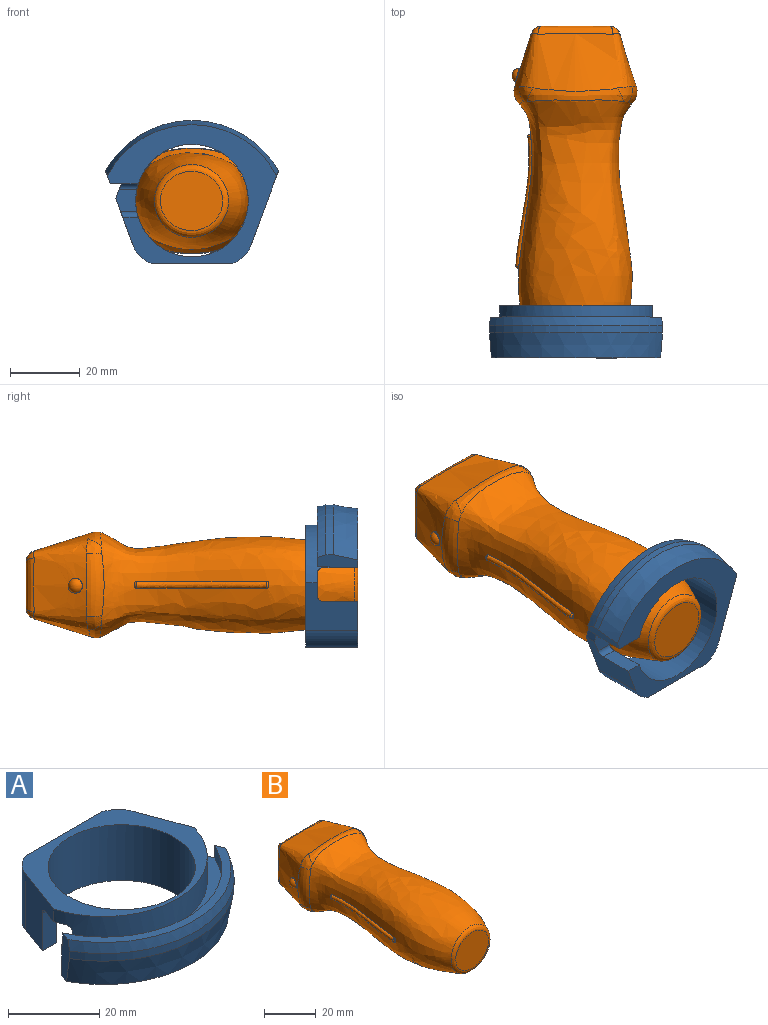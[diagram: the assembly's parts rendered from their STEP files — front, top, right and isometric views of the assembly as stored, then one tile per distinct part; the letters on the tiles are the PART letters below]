
ASSEMBLY  parts=2 mates=1
PART A: 21 faces, bbox 50.6x40.9x15 mm
  f0: plane 43.64x35.03mm, normal (0,0,1), area 388.7mm2, adj f2,f14,f16,f17,f18,f19,f20
  f1: cylinder r=28.52mm len=49.53mm, axis (0,0,1), area 121.9mm2, adj f7,f8,f15,f16
  f2: cylinder r=22.68mm len=43.64mm, axis (0,0,1), area 377.4mm2, adj f0,f5,f10,f11,f13,f16,f17
  f3: plane 48.95x17.13mm, normal (0,0,1), area 120.6mm2, adj f4,f7,f15,f16
  f4: cylinder r=25.86mm len=47.02mm, axis (0,0,1), area 200.9mm2, adj f3,f5,f15,f16
  f5: plane 47.02x19.67mm, normal (0,0,1), area 180.1mm2, adj f2,f4,f13,f15,f16
  f6: plane 48.44x39.68mm, normal (0,0,-1), area 607.5mm2, adj f8,f12,f13,f14,f15,f16,f17,f18
  f7: cone r=28.52mm half-angle=14deg, axis (0,0,-1), area 156.7mm2, adj f1,f3,f15,f16
  f8: cone r=28.52mm half-angle=9.5deg, axis (0,0,1), area 430.8mm2, adj f1,f6,f15,f16
  f9: cylinder r=1.59mm len=5.03mm, axis (-1,0,0), area 11.2mm2, adj f10,f12,f14,f17
  f10: plane 6.48x6.03mm, normal (0,0,-1), area 33.8mm2, adj f2,f9,f11,f14,f17
  f11: cylinder r=1.59mm len=5.51mm, axis (-1,0,0), area 12.2mm2, adj f2,f10,f13,f14
  f12: plane 10.07x4.44mm, normal (0,-1,0), area 44.8mm2, adj f6,f9,f14,f17
  f13: plane 10.07x8.01mm, normal (0,1,0), area 74.9mm2, adj f2,f5,f6,f11,f14,f15
  f14: cylinder r=16.12mm len=32.23mm, axis (0,0,-1), area 1401.8mm2, adj f0,f6,f9,f10,f11,f12,f13
  f15: plane 11.69x3.74mm, normal (-0.94,0.35,0), area 38.6mm2, adj f1,f3,f4,f5,f6,f7,f8,f13
  f16: plane 21.7x14.97mm, normal (0.94,0.35,0), area 294.9mm2, adj f0,f1,f2,f3,f4,f5,f6,f7
  f17: plane 14.96x13.72mm, normal (-0.94,0.35,0), area 152.2mm2, adj f0,f2,f6,f9,f10,f12,f20
  f18: cylinder r=7.94mm len=14.96mm, axis (0,0,-1), area 107.8mm2, adj f0,f6,f16,f19
  f19: plane 23.44x14.96mm, normal (0,1,0), area 350.6mm2, adj f0,f6,f18,f20
  f20: cylinder r=7.94mm len=14.96mm, axis (0,0,-1), area 107.8mm2, adj f0,f6,f17,f19
PART B: 39 faces, bbox 36.7x95x30.5 mm
  f0: bspline ~73.26x33.11mm, area 6402mm2, adj f1,f2,f3,f4,f5,f6,f7,f30
  f1: bspline ~2.01x1.21mm, area 2mm2, adj f0,f2,f5,f6
  f2: bspline ~38.45x6.12mm, area 113.8mm2, adj f0,f1,f3,f5
  f3: bspline ~2.01x1.22mm, area 1.9mm2, adj f0,f2,f4,f5
  f4: plane 1.01x0.56mm, normal (-0.2,-0.98,0), area 0.4mm2, adj f0,f3,f5
  f5: bspline ~38.44x3.99mm, area 45.3mm2, adj f0,f1,f2,f3,f4,f6
  f6: plane 0.98x0.43mm, normal (0,1,0), area 0.3mm2, adj f0,f1,f5
  f7: bspline ~5.49x5.15mm, area 20mm2, adj f0,f8,f30,f36
  f8: bspline ~35.73x29.82mm, area 1555.8mm2, adj f7,f9,f14,f15,f16,f17,f21,f22
  f9: bspline ~1.78x0.64mm, area 0.1mm2, adj f8,f10,f14,f16
  f10: torus R=1.78mm, axis (0.98,-0.22,0), area 1.2mm2, adj f9,f11,f12,f13,f15
  f11: sphere r=2.19mm, area 19.9mm2, adj f10,f13
  f12: cylinder r=2.08mm len=4.15mm, axis (0.98,-0.22,0), area 0mm2, adj f10,f16
  f13: bspline ~1.37x0.16mm, area 0mm2, adj f10,f11,f14
  f14: bspline ~0.9x0.11mm, area 0mm2, adj f8,f9,f13,f15
  f15: bspline ~1.38x0.77mm, area 0.1mm2, adj f8,f10,f14,f16
  f16: bspline ~4.24x3.75mm, area 0.8mm2, adj f8,f9,f12,f15
  f17: bspline ~26x3.24mm, area 79.8mm2, adj f8,f18,f19,f20,f21,f29
  f18: bspline ~2.88x2.87mm, area 4.3mm2, adj f17,f28,f29
  f19: plane 19.6x13.61mm, normal (0,1,0), area 263.4mm2, adj f17,f22,f25,f28
  f20: bspline ~2.88x2.87mm, area 4.3mm2, adj f17,f21,f22
  f21: bspline ~1.84x1.83mm, area 0.1mm2, adj f8,f17,f20
  f22: bspline ~20.51x3.3mm, area 55.4mm2, adj f8,f19,f20,f23
  f23: bspline ~2.88x2.87mm, area 4.3mm2, adj f22,f24,f25
  f24: bspline ~1.84x1.83mm, area 0.1mm2, adj f8,f23,f25
  f25: bspline ~29.81x3.28mm, area 79.9mm2, adj f8,f19,f23,f24,f26,f27
  f26: bspline ~2.88x2.87mm, area 4.3mm2, adj f25,f27,f28
  f27: bspline ~1.84x1.83mm, area 0.1mm2, adj f8,f25,f26
  f28: bspline ~20.51x3.3mm, area 55.4mm2, adj f8,f18,f19,f26
  f29: bspline ~1.84x1.83mm, area 0.1mm2, adj f8,f17,f18
  f30: bspline ~27.54x4.29mm, area 82mm2, adj f0,f7,f8,f31
  f31: bspline ~5.52x5.15mm, area 20.9mm2, adj f0,f8,f30,f32
  f32: bspline ~18.94x5.15mm, area 95.2mm2, adj f0,f8,f31,f33
  f33: bspline ~6.57x5.49mm, area 20mm2, adj f0,f8,f32,f34
  f34: bspline ~27.71x4.4mm, area 81.7mm2, adj f0,f8,f33,f35
  f35: bspline ~5.8x5.25mm, area 20mm2, adj f0,f8,f34,f36
  f36: bspline ~19.31x5.16mm, area 96.4mm2, adj f0,f7,f8,f35
  f37: bspline ~21.22x20.84mm, area 142.1mm2, adj f0,f38
  f38: plane 17.87x16.96mm, normal (0,-1,0), area 237.6mm2, adj f37
PLACE A rot(axis=(-1,0,0),90deg) t=(45.93,62.87,-28.55)mm
PLACE B t=(45.79,47.91,-23.05)mm
MATE planar A.f6 <-> B.f38  axis (0,-1,0) through (70.15,47.91,-15.87)mm
